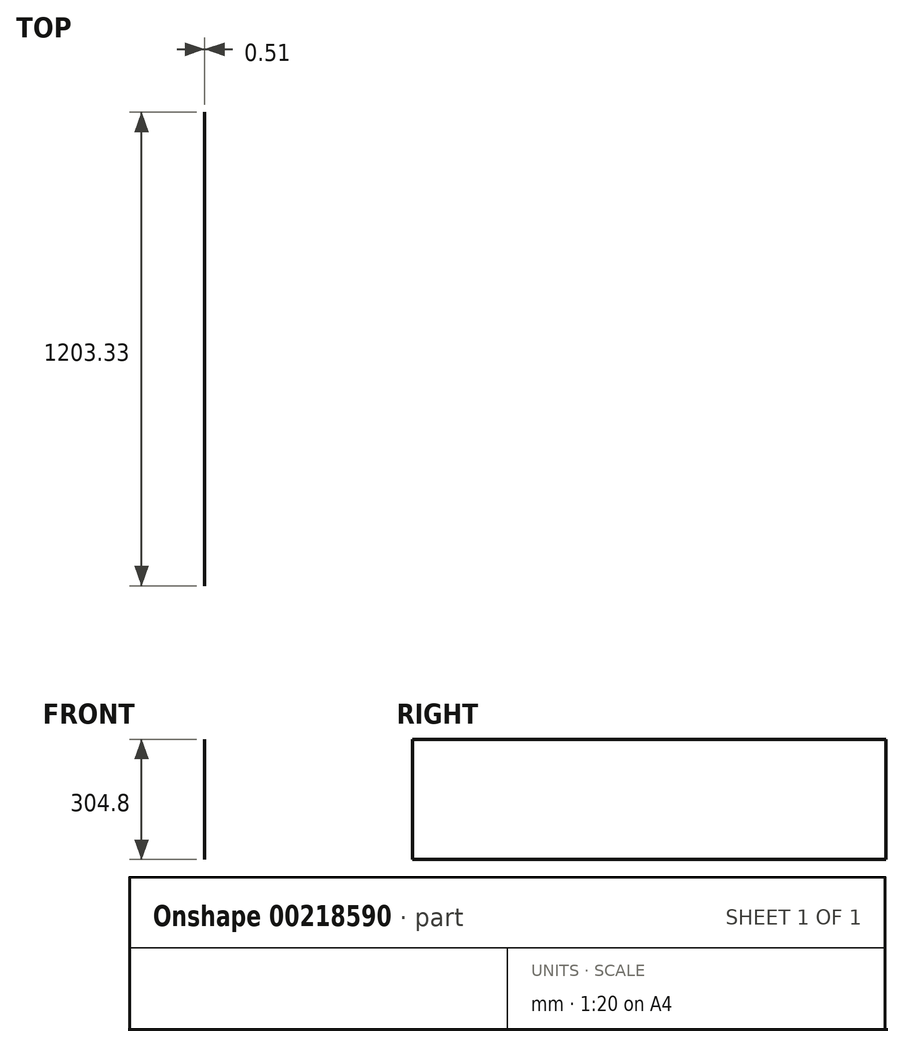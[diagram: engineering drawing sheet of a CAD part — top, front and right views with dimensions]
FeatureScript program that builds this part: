
annotation { "Feature Type Name" : "Feature", "Feature Type Description" : "" }
export const myFeature = defineFeature(function(context is Context, id is Id, definition is map)
    precondition{}
    {
        {
            var Q0;
            Q0=qCreatedBy(makeId("Right.planeOp"),FACE);
            var sketch = newSketch(context, id + "F0", { "sketchPlane" : qUnion([Q0])});
            skLineSegment(sketch, "E0.bottom", {"start": v(0, 0) * mm, "end": v(-1203.32, 0) * mm});
            skLineSegment(sketch, "E0.top", {"start": v(0, 304.8) * mm, "end": v(-1203.33, 304.8) * mm});
            skLineSegment(sketch, "E0.left", {"start": v(0, 0) * mm, "end": v(0, 304.8) * mm});
            skLineSegment(sketch, "E0.right", {"start": v(-1203.33, 0) * mm, "end": v(-1203.33, 304.8) * mm});
            skSolve(sketch);
        }
        {
            var Q0;
            Q0=makeQuery(id+"F0.imprint","IMPRINT",FACE,{"disambiguationData":[TD([[makeQuery(id+"F0.imprint","IMPRINT",EDGE,{"derivedFrom":sQuery(id+"F0.wireOp",EDGE,"E0.bottom")}),-1.0]])]});
            extrude(context, id + "F1", {"entities" : qUnion([Q0]), "depth" : 0.5 * mm});
        }
    });
